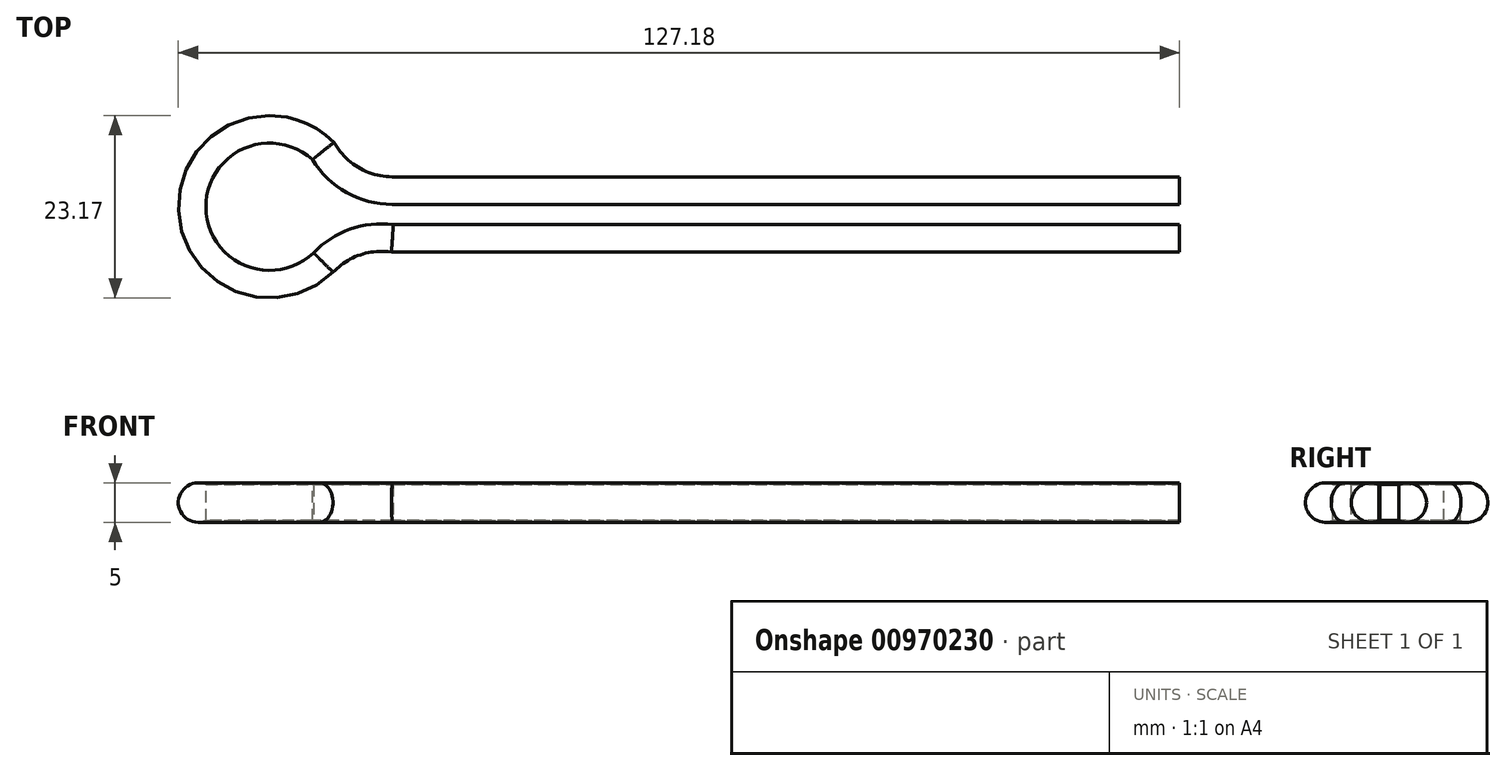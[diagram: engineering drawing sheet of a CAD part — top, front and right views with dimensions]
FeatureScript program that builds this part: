
annotation { "Feature Type Name" : "Feature", "Feature Type Description" : "" }
export const myFeature = defineFeature(function(context is Context, id is Id, definition is map)
    precondition{}
    {
        {
            var Q0;
            Q0=qCreatedBy(makeId("Top.planeOp"),FACE);
            var sketch = newSketch(context, id + "F0", { "sketchPlane" : qUnion([Q0])});
            skLineSegment(sketch, "E0", {"start": v(0, 0) * mm, "end": v(-100, 0) * mm});
            skArc(sketch, "E1", {"start": v(-108.65, 4.98) * mm, "mid": v(-104.99, 1.33) * mm, "end": v(-100, 0) * mm});
            skArc(sketch, "E2", {"start": v(-108.65, 4.98) * mm, "mid": v(-125.6, -2.22) * mm, "end": v(-108.65, -9.41) * mm});
            skArc(sketch, "E3", {"start": v(-100, -6.39) * mm, "mid": v(-104.7, -6.85) * mm, "end": v(-108.65, -9.41) * mm});
            skLineSegment(sketch, "E4", {"start": v(-100, -6.39) * mm, "end": v(0, -6.39) * mm});
            skSolve(sketch);
        }
        {
            var Q0;
            Q0=qCreatedBy(makeId("Right.planeOp"),FACE);
            var sketch = newSketch(context, id + "F1", { "sketchPlane" : qUnion([Q0])});
            skLineSegment(sketch, "E5", {"start": v(-1.91, 1.66) * mm, "end": v(-1.91, -2.92) * mm});
            skArc(sketch, "E6", {"start": v(-1.91, -2.92) * mm, "mid": v(1.59, -0.63) * mm, "end": v(-1.91, 1.66) * mm});
            skSolve(sketch);
        }
        {
            var Q0;
            Q0=makeQuery(id+"F1.imprint","IMPRINT",FACE,{"disambiguationData":[TD([[makeQuery(id+"F1.imprint","IMPRINT",EDGE,{"derivedFrom":sQuery(id+"F1.wireOp",EDGE,"E5")}),1.0]])]});
            var Q1;
            Q1=sQuery(id+"F0.wireOp",EDGE,"E0");
            var Q2;
            Q2=sQuery(id+"F0.wireOp",EDGE,"E1");
            var Q3;
            Q3=sQuery(id+"F0.wireOp",EDGE,"E2");
            var Q4;
            Q4=sQuery(id+"F0.wireOp",EDGE,"E4");
            var Q5;
            Q5=sQuery(id+"F0.wireOp",EDGE,"E3");
            sweep(context, id + "F2", {"profiles" : qUnion([Q0]), "path" : qUnion([Q1, Q2, Q3, Q4, Q5])});
        }
    });
